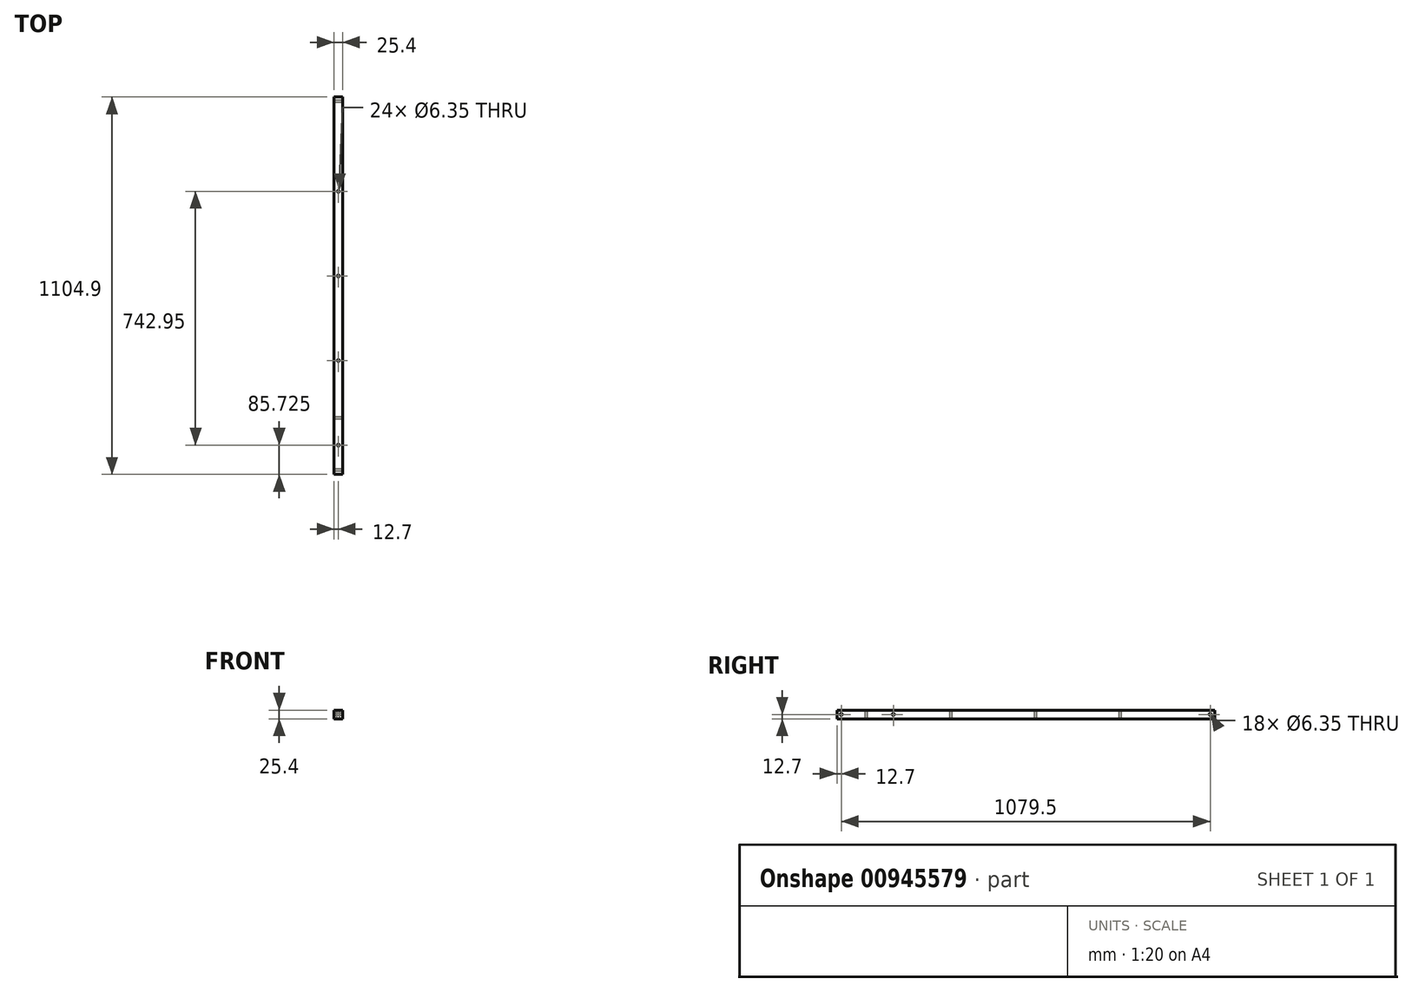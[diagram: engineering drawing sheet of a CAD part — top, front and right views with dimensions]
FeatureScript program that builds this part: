
annotation { "Feature Type Name" : "Feature", "Feature Type Description" : "" }
export const myFeature = defineFeature(function(context is Context, id is Id, definition is map)
    precondition{}
    {
        {
            var Q0;
            Q0=qCreatedBy(makeId("Front.planeOp"),FACE);
            var sketch = newSketch(context, id + "F0", { "sketchPlane" : qUnion([Q0])});
            skLineSegment(sketch, "E0.bottom", {"start": v(12.7, 12.7) * mm, "end": v(-12.7, 12.7) * mm});
            skLineSegment(sketch, "E0.top", {"start": v(12.7, -12.7) * mm, "end": v(-12.7, -12.7) * mm});
            skLineSegment(sketch, "E0.left", {"start": v(12.7, 12.7) * mm, "end": v(12.7, -12.7) * mm});
            skLineSegment(sketch, "E0.right", {"start": v(-12.7, 12.7) * mm, "end": v(-12.7, -12.7) * mm});
            skPoint(sketch, "E0.middle", {"position": v(0, 0) * mm});
            skSolve(sketch);
        }
        {
            var Q0;
            Q0=makeQuery(id+"F0.imprint","IMPRINT",FACE,{"disambiguationData":[TD([[makeQuery(id+"F0.imprint","IMPRINT",EDGE,{"derivedFrom":sQuery(id+"F0.wireOp",EDGE,"E0.bottom")}),1.0]])]});
            extrude(context, id + "F1", {"entities" : qUnion([Q0]), "oppositeDirection" : true, "depth" : 1104.9 * mm, "offsetDistance" : 25 * mm});
        }
        {
            var Q0;
            Q0=makeQuery(id+"F1.opExtrude","SWEPT_FACE",FACE,{"disambiguationData":[OSD([sQuery(id+"F0.wireOp",EDGE,"E0.right")])]});
            var sketch = newSketch(context, id + "F2", { "sketchPlane" : qUnion([Q0])});
            skCircle(sketch, "E1", {"center": v(-12.7, 0) * mm, "radius": 3.18 * mm});
            skCircle(sketch, "E2", {"center": v(-165.1, 0) * mm, "radius": 3.18 * mm});
            skCircle(sketch, "E3", {"center": v(-1092.2, 0) * mm, "radius": 3.18 * mm});
            skSolve(sketch);
        }
        {
            var Q0;
            Q0=qSketchRegion(id+"F2",true);
            var Q1;
            Q1=makeQuery(id+"F1.opExtrude","SWEPT_FACE",FACE,{"disambiguationData":[OSD([sQuery(id+"F0.wireOp",EDGE,"E0.left")])]});
            extrude(context, id + "F3", {"entities" : qUnion([Q0]), "operationType" : NewBodyOperationType.REMOVE, "endBound" : BoundingType.UP_TO_SURFACE, "oppositeDirection" : true, "depth" : 25 * mm, "endBoundEntityFace" : qUnion([Q1]), "offsetDistance" : 25 * mm});
        }
        {
            var Q0;
            Q0=makeQuery(id+"F1.opExtrude","SWEPT_FACE",FACE,{"disambiguationData":[OSD([sQuery(id+"F0.wireOp",EDGE,"E0.bottom")])]});
            var sketch = newSketch(context, id + "F4", { "sketchPlane" : qUnion([Q0])});
            skCircle(sketch, "E4", {"center": v(0, 85.73) * mm, "radius": 3.18 * mm});
            skCircle(sketch, "E5", {"center": v(0, 333.38) * mm, "radius": 3.18 * mm});
            skCircle(sketch, "E6", {"center": v(0, 581.03) * mm, "radius": 3.18 * mm});
            skCircle(sketch, "E7", {"center": v(0, 828.68) * mm, "radius": 3.18 * mm});
            skSolve(sketch);
        }
        {
            var Q0;
            Q0=qSketchRegion(id+"F4",true);
            var Q1;
            Q1=makeQuery(id+"F1.opExtrude","SWEPT_FACE",FACE,{"disambiguationData":[OSD([sQuery(id+"F0.wireOp",EDGE,"E0.top")])]});
            extrude(context, id + "F5", {"entities" : qUnion([Q0]), "operationType" : NewBodyOperationType.REMOVE, "endBound" : BoundingType.UP_TO_SURFACE, "oppositeDirection" : true, "depth" : 25 * mm, "endBoundEntityFace" : qUnion([Q1]), "offsetDistance" : 25 * mm});
        }
    });
